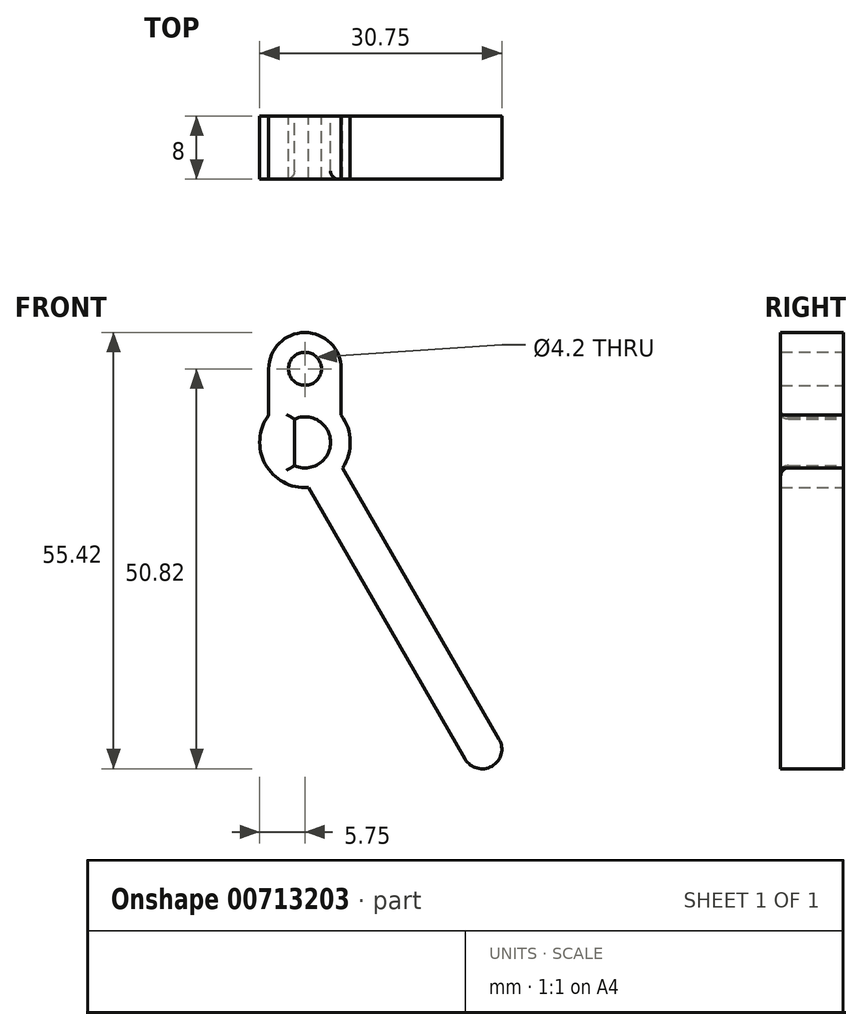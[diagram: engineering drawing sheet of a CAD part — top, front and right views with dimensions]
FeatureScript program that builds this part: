
annotation { "Feature Type Name" : "Feature", "Feature Type Description" : "" }
export const myFeature = defineFeature(function(context is Context, id is Id, definition is map)
    precondition{}
    {
        {
            var Q0;
            Q0=qCreatedBy(makeId("Front.planeOp"),FACE);
            var sketch = newSketch(context, id + "F0", { "sketchPlane" : qUnion([Q0])});
            skCircle(sketch, "E0", {"center": v(0, 0) * mm, "radius": 3.25 * mm});
            skLineSegment(sketch, "E1", {"start": v(-1.35, 2.96) * mm, "end": v(-1.35, -2.96) * mm});
            skCircle(sketch, "E2", {"center": v(0, 0) * mm, "radius": 5.75 * mm});
            skCircle(sketch, "E3", {"center": v(0, 9.35) * mm, "radius": 2.1 * mm});
            skArc(sketch, "E4", {"start": v(-4.6, 9.35) * mm, "mid": v(0, 13.95) * mm, "end": v(4.6, 9.35) * mm});
            skLineSegment(sketch, "E5", {"start": v(0, 3.25) * mm, "end": v(0, 5.75) * mm, "construction": true});
            skLineSegment(sketch, "E6", {"start": v(0, 11.45) * mm, "end": v(0, 13.95) * mm, "construction": true});
            skLineSegment(sketch, "E7", {"start": v(-4.6, 9.35) * mm, "end": v(-4.6, 3.45) * mm});
            skLineSegment(sketch, "E8", {"start": v(4.6, 9.35) * mm, "end": v(4.6, 3.45) * mm});
            skLineSegment(sketch, "E9", {"start": v(0, 0) * mm, "end": v(22.5, -38.97) * mm, "construction": true});
            skCircle(sketch, "E10", {"center": v(22.5, -38.97) * mm, "radius": 2.5 * mm});
            skLineSegment(sketch, "E11", {"start": v(20.33, -40.22) * mm, "end": v(0.42, -5.73) * mm});
            skLineSegment(sketch, "E12", {"start": v(4.75, -3.23) * mm, "end": v(24.67, -37.72) * mm});
            skLineSegment(sketch, "E13", {"start": v(22.5, -38.97) * mm, "end": v(24.67, -37.72) * mm, "construction": true});
            skLineSegment(sketch, "E14", {"start": v(22.5, -38.97) * mm, "end": v(20.33, -40.22) * mm, "construction": true});
            skSolve(sketch);
        }
        {
            var Q0;
            Q0=makeQuery(id+"F0.imprint","IMPRINT",FACE,{"disambiguationData":[TD([[makeQuery(id+"F0.imprint","IMPRINT",EDGE,{"derivedFrom":sQuery(id+"F0.wireOp",EDGE,"E3")}),-1.0]])]});
            var Q1;
            {var subQ4=sQuery(id+"F0.wireOp",EDGE,"E1");var subQ5=sQuery(id+"F0.wireOp",EDGE,"E0");var subQ6=makeQuery(id+"F0.imprint","INTERSECT",VERTEX,{"disambiguationData":[OD(0.0)],"derivedFrom":[subQ5,subQ4]});Q1=makeQuery(id+"F0.imprint","IMPRINT",FACE,{"disambiguationData":[TD([[makeQuery(id+"F0.imprint","IMPRINT",EDGE,{"disambiguationData":[TD([[subQ6,-1.0]])],"derivedFrom":subQ5}),-1.0]])]});}
            var Q2;
            {var subQ0=sQuery(id+"F0.wireOp",EDGE,"E1");Q2=makeQuery(id+"F0.imprint","IMPRINT",FACE,{"disambiguationData":[TD([[makeQuery(id+"F0.imprint","IMPRINT",EDGE,{"derivedFrom":subQ0}),-1.0]])]});}
            var Q3;
            {var subQ0=sQuery(id+"F0.wireOp",EDGE,"E11");Q3=makeQuery(id+"F0.imprint","IMPRINT",FACE,{"disambiguationData":[TD([[makeQuery(id+"F0.imprint","IMPRINT",EDGE,{"derivedFrom":subQ0}),-1.0]])]});}
            var Q4;
            {var subQ0=sQuery(id+"F0.wireOp",EDGE,"E10");var subQ1=makeQuery(id+"F0.imprint","INTERSECT",VERTEX,{"derivedFrom":[subQ0,sQuery(id+"F0.wireOp",EDGE,"E11")]});Q4=makeQuery(id+"F0.imprint","IMPRINT",FACE,{"disambiguationData":[TD([[makeQuery(id+"F0.imprint","IMPRINT",EDGE,{"disambiguationData":[TD([[subQ1,1.0]])],"derivedFrom":subQ0}),1.0]])]});}
            extrude(context, id + "F1", {"entities" : qUnion([Q0, Q1, Q2, Q3, Q4]), "depth" : 8 * mm, "offsetDistance" : 25 * mm});
        }
        {
            var Q0;
            Q0=makeQuery(id+"F1.opExtrude","CAP_EDGE",EDGE,{"disambiguationData":[OSD([sQuery(id+"F0.wireOp",EDGE,"E0")])],"isStart":false});
            var Q1;
            Q1=makeQuery(id+"F1.opExtrude","CAP_EDGE",EDGE,{"disambiguationData":[OSD([sQuery(id+"F0.wireOp",EDGE,"E1")])],"isStart":false});
            fillet(context, id + "F2", {"entities" : qUnion([Q0, Q1]), "radius" : 1 * mm, "tangentPropagation" : true, "allowEdgeOverflow" : false});
        }
    });
